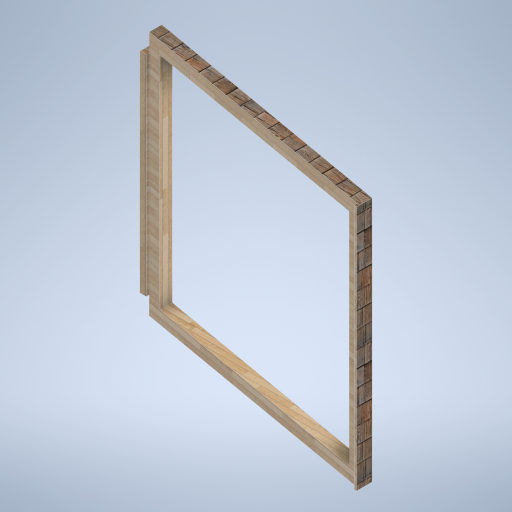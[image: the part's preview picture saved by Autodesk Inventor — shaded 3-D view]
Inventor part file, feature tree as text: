
AUTODESK INVENTOR PART (.ipt)
format: ipt  version: 2024.2 (Build 282272000, 272)  size: 361,472 bytes
history: native  units: in
note: dims shown in document units (in); Inventor stores cm internally (conversion verified against a paired STEP export)
features: sketch x9, plane x4, other x3
ambient origin geometry x8: Origin, YZ Plane, XZ Plane, XY Plane, X Axis, Y Axis, Z Axis, Center Point
bodies: Solid1 (feature_tree)
feature tree (16):
  other  "eave_frame_side.ipt"
  other  "Solid1::eave_frame_side.ipt"
  other  "TaggingFeature1"
  sketch  "Sketch1"  dims[d0=0.3937in]
  sketch  "Sketch2"
  sketch  "Sketch3"
  sketch  "Sketch4"
  sketch  "Sketch5"
  sketch  "Sketch6"
  sketch  "Sketch7"
  sketch  "Sketch8"
  sketch  "Sketch9"
  plane  "Work Plane1"
  plane  "Work Plane2"
  plane  "Work Plane3"
  plane  "Work Plane4"
